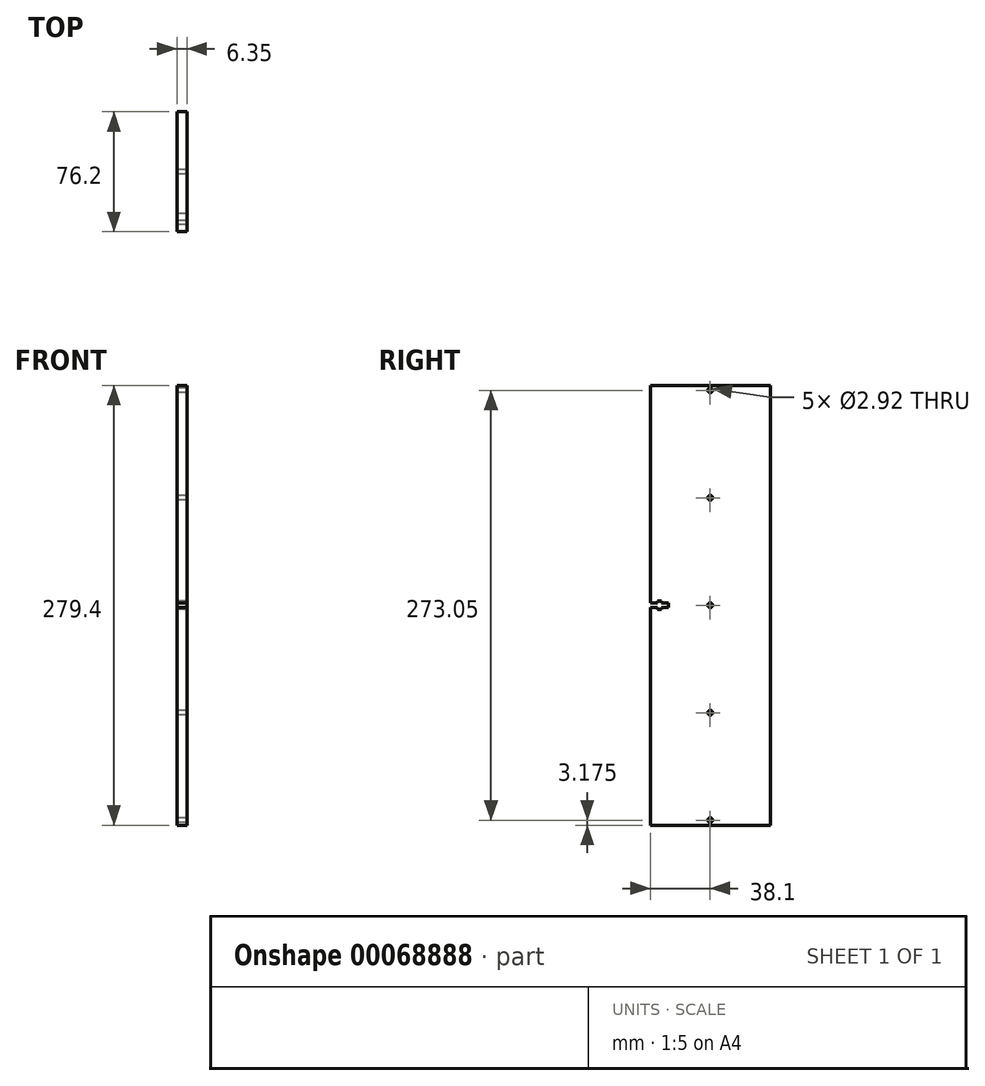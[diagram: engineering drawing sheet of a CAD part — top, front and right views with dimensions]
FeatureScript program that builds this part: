
annotation { "Feature Type Name" : "Feature", "Feature Type Description" : "" }
export const myFeature = defineFeature(function(context is Context, id is Id, definition is map)
    precondition{}
    {
        {
            var Q0;
            Q0=qCreatedBy(makeId("Right.planeOp"),FACE);
            var sketch = newSketch(context, id + "F0", { "sketchPlane" : qUnion([Q0])});
            skLineSegment(sketch, "E0.rect.bottom", {"start": v(-38.1, 139.7) * mm, "end": v(38.1, 139.7) * mm});
            skLineSegment(sketch, "E0.rect.top", {"start": v(-38.1, -139.7) * mm, "end": v(38.1, -139.7) * mm});
            skLineSegment(sketch, "E0.rect.left", {"start": v(-38.1, 139.7) * mm, "end": v(-38.1, 1.46) * mm});
            skLineSegment(sketch, "E0.rect.right", {"start": v(38.1, 139.7) * mm, "end": v(38.1, -139.7) * mm});
            skPoint(sketch, "E0.rect.middle", {"position": v(0, 0) * mm});
            skLineSegment(sketch, "E1", {"start": v(38.1, 136.53) * mm, "end": v(-38.1, 136.53) * mm, "construction": true});
            skLineSegment(sketch, "E2", {"start": v(-34.92, 139.7) * mm, "end": v(-34.92, -139.7) * mm, "construction": true});
            skLineSegment(sketch, "E3", {"start": v(38.1, -136.53) * mm, "end": v(-38.1, -136.53) * mm, "construction": true});
            skLineSegment(sketch, "E4", {"start": v(0, 136.53) * mm, "end": v(0, 135.06) * mm, "construction": true});
            skCircle(sketch, "E5", {"center": v(0, 136.53) * mm, "radius": 1.46 * mm});
            skCircle(sketch, "E6", {"center": v(0, -136.53) * mm, "radius": 1.46 * mm});
            skLineSegment(sketch, "E7", {"start": v(-38.1, 0) * mm, "end": v(38.1, 0) * mm, "construction": true});
            skLineSegment(sketch, "E8.0", {"start": v(-38.1, -1.46) * mm, "end": v(38.1, -1.46) * mm, "construction": true});
            skLineSegment(sketch, "E9.0", {"start": v(-38.1, 1.46) * mm, "end": v(38.1, 1.46) * mm, "construction": true});
            skLineSegment(sketch, "E10", {"start": v(-33.65, 1.46) * mm, "end": v(-33.65, -1.46) * mm, "construction": true});
            skLineSegment(sketch, "E11.0", {"start": v(-38.1, 2.73) * mm, "end": v(38.1, 2.73) * mm, "construction": true});
            skLineSegment(sketch, "E12.0", {"start": v(-38.1, -2.73) * mm, "end": v(38.1, -2.73) * mm, "construction": true});
            skLineSegment(sketch, "E13", {"start": v(-38.1, 1.46) * mm, "end": v(-33.65, 1.46) * mm});
            skLineSegment(sketch, "E14", {"start": v(-33.65, 1.46) * mm, "end": v(-33.65, 2.73) * mm});
            skLineSegment(sketch, "E15", {"start": v(-33.65, 2.73) * mm, "end": v(-31.11, 2.73) * mm});
            skLineSegment(sketch, "E16", {"start": v(-31.11, 2.73) * mm, "end": v(-31.11, 1.46) * mm});
            skLineSegment(sketch, "E17", {"start": v(-31.11, -2.73) * mm, "end": v(-33.65, -2.73) * mm});
            skLineSegment(sketch, "E18", {"start": v(-33.65, -2.73) * mm, "end": v(-33.65, -1.46) * mm});
            skLineSegment(sketch, "E19", {"start": v(-33.65, -1.46) * mm, "end": v(-38.1, -1.46) * mm});
            skLineSegment(sketch, "E20.trimOffspring", {"start": v(-38.1, -1.46) * mm, "end": v(-38.1, -139.7) * mm});
            skLineSegment(sketch, "E21", {"start": v(-31.11, 1.46) * mm, "end": v(-26.67, 1.46) * mm});
            skLineSegment(sketch, "E22", {"start": v(-26.67, 1.46) * mm, "end": v(-26.67, -1.46) * mm});
            skLineSegment(sketch, "E23", {"start": v(-26.67, -1.46) * mm, "end": v(-31.11, -1.46) * mm});
            skLineSegment(sketch, "E24.trimOffspring", {"start": v(-31.11, -1.46) * mm, "end": v(-31.11, -2.73) * mm});
            skPoint(sketch, "E25.orphan", {"position": v(-31.11, -11.24) * mm});
            skCircle(sketch, "E26", {"center": v(0, 0) * mm, "radius": 1.46 * mm});
            skLineSegment(sketch, "E27.trimOffspring", {"start": v(0, 0) * mm, "end": v(0, -136.53) * mm, "construction": true});
            skCircle(sketch, "E28", {"center": v(0, -68.26) * mm, "radius": 1.46 * mm});
            skCircle(sketch, "E29.MirrorC", {"center": v(0, 68.26) * mm, "radius": 1.46 * mm});
            skSolve(sketch);
        }
        {
            var Q0;
            Q0=makeQuery(id+"F0.imprint","IMPRINT",FACE,{"disambiguationData":[TD([[makeQuery(id+"F0.imprint","IMPRINT",EDGE,{"derivedFrom":sQuery(id+"F0.wireOp",EDGE,"E0.rect.bottom")}),-1.0]])]});
            extrude(context, id + "F1", {"entities" : qUnion([Q0]), "depth" : 6.35 * mm});
        }
    });
